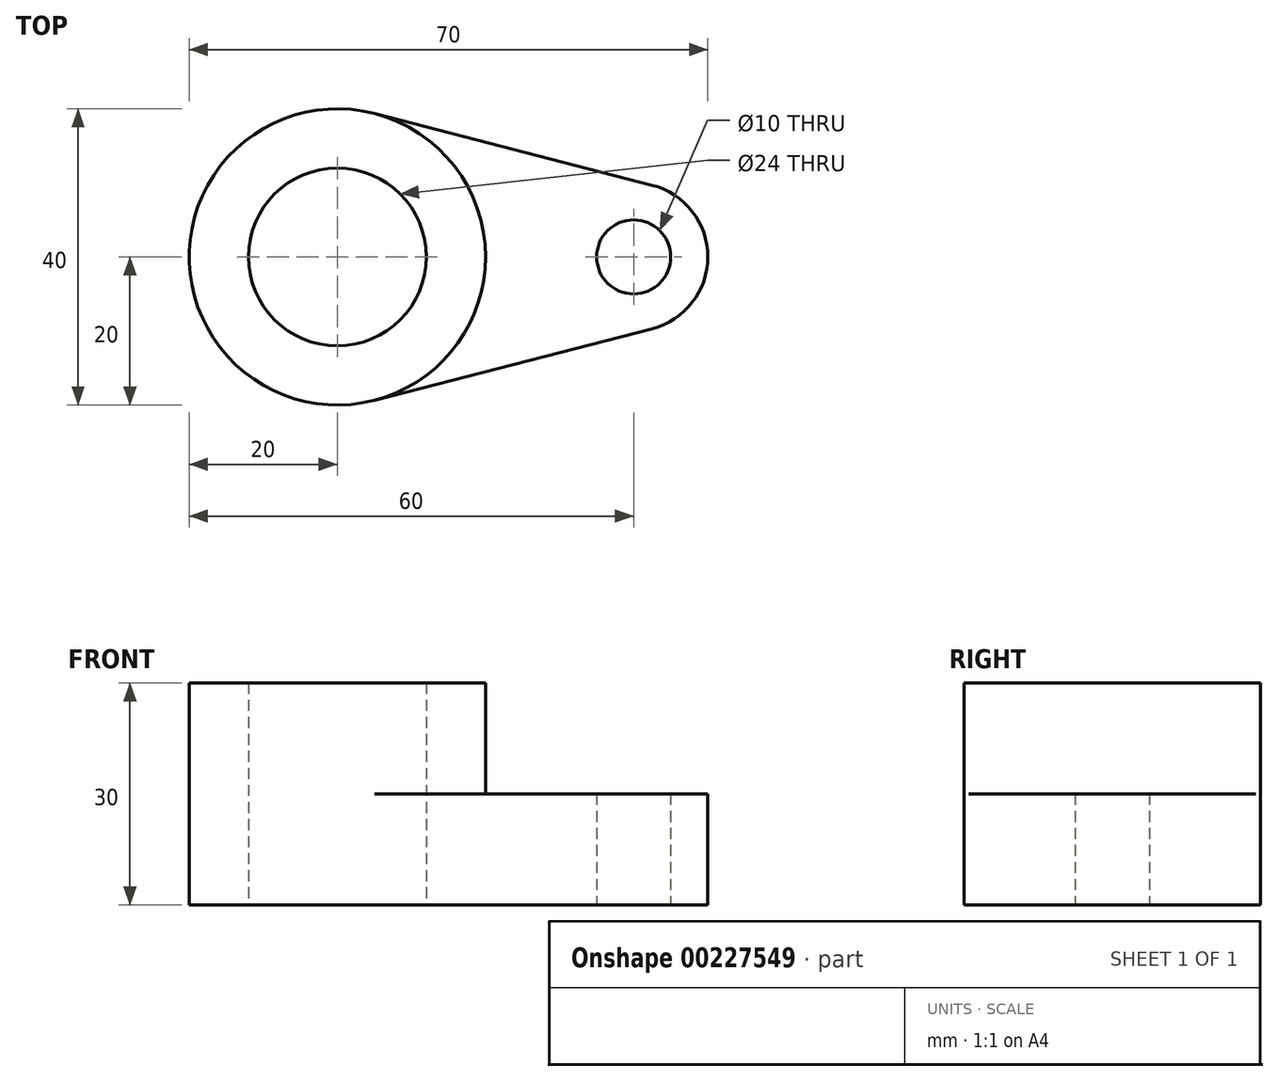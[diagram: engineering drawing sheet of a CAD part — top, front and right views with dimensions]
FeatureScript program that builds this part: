
annotation { "Feature Type Name" : "Feature", "Feature Type Description" : "" }
export const myFeature = defineFeature(function(context is Context, id is Id, definition is map)
    precondition{}
    {
        {
            var Q0;
            Q0=qCreatedBy(makeId("Top.planeOp"),FACE);
            var sketch = newSketch(context, id + "F0", { "sketchPlane" : qUnion([Q0])});
            skCircle(sketch, "E0", {"center": v(0, 0) * mm, "radius": 20 * mm});
            skCircle(sketch, "E1", {"center": v(40, 0) * mm, "radius": 5 * mm});
            skArc(sketch, "E2", {"start": v(42.5, -9.68) * mm, "mid": v(50, 0) * mm, "end": v(42.5, 9.68) * mm});
            skLineSegment(sketch, "E3", {"start": v(5, 19.36) * mm, "end": v(42.5, 9.68) * mm});
            skLineSegment(sketch, "E4", {"start": v(5, -19.36) * mm, "end": v(42.5, -9.68) * mm});
            skCircle(sketch, "E5", {"center": v(0, 0) * mm, "radius": 12 * mm});
            skSolve(sketch);
        }
        {
            var Q0;
            Q0=makeQuery(id+"F0.imprint","IMPRINT",FACE,{"disambiguationData":[TD([[makeQuery(id+"F0.imprint","IMPRINT",EDGE,{"derivedFrom":sQuery(id+"F0.wireOp",EDGE,"E1")}),-1.0]])]});
            extrude(context, id + "F1", {"entities" : qUnion([Q0]), "depth" : 15 * mm});
        }
        {
            var Q0;
            Q0=makeQuery(id+"F0.imprint","IMPRINT",FACE,{"disambiguationData":[TD([[makeQuery(id+"F0.imprint","IMPRINT",EDGE,{"derivedFrom":sQuery(id+"F0.wireOp",EDGE,"E5")}),-1.0]])]});
            extrude(context, id + "F2", {"entities" : qUnion([Q0]), "operationType" : NewBodyOperationType.ADD, "depth" : 30 * mm});
        }
    });
